# Revit family: Haworth_JiveTable_HalfPebbleLegs
name_source: partatom
category: Furniture Systems
revit_build: Autodesk Revit 2018 (Build: 20170223_1515(x64)
units: mm (PartAtom-declared; Revit-internal decimal feet)

## family parameters
Always vertical = Yes
Cut with Voids When Loaded = No
OmniClass Number = 23.40.70.14.64.21
OmniClass Title = Systems Furniture
Part Type = Normal
Room Calculation Point = No
Round Connector Dimension = Use Diameter
Shared = No
Work Plane-Based = No

## types (16) — shared parameters
Actual Height = 29"
Assembly Code = E2020200
Custom Size = No
Height = 29"
Leg Height = 27 13/16"
Manufacturer = Haworth, Inc.
Max. Depth = 60"
Max. Height = 29"
Max. Width = 60"
Min. Depth = 42"
Min. Height = 29"
Min. Width = 42"
Model = Haworth Jive
Revision Number = 0
Size = Verify Final Dim. w/ Haworth
Standard Depths = 42, 48, 54, 60 in.
Standard Heights = 29 in.
Standard Widths = 42, 48, 54, 60 in.
Table Thickness = 1 3/16"
URL = http://www.haworth.com
URL - Product = http://www.haworth.com
Warranty = http://www.haworth.com

## per-type parameters (varying)
| type | Actual Depth | Actual Width | Casters | Close Legs | Depth | Description | Far Legs | Glides | Post Extruded Base | Post Round Base | Table Radius | Vert. Leg Center | Width |
| 42d 42w 29h - Post Extruded Base - With Glides | 42" | 42" | No | 7" | 42" | Haworth Jive Table Half Pebble Legs - 42d 42w 29h - Post Extruded Bases - With Glides | 31" | Yes | Yes | No | 21" | 11" | 42" |
| 42d 42w 29h - Post Extruded Base - With Casters | 42" | 42" | Yes | 7" | 42" | Haworth Jive Table Half Pebble Legs - 42d 42w 29h - Post Extruded Base - With Casters | 31" | No | Yes | No | 21" | 11" | 42" |
| 48d 48w 29h - Post Extruded Base - With Glides | 48" | 48" | No | 8" | 48" | Haworth Jive Table Half Pebble Legs - 48d 48w 29h - Post Extruded Base - With Glides | 36" | Yes | Yes | No | 24" | 15" | 48" |
| 48d 48w 29h - Post Extruded Base - With Casters | 48" | 48" | Yes | 8" | 48" | Haworth Jive Table Half Pebble Legs - 48d 48w 29h - Post Extruded Base - With Casters | 36" | No | Yes | No | 24" | 15" | 48" |
| 54d 54w 29h - Post Extruded Base - With Glides | 54" | 54" | No | 10" | 54" | Haworth Jive Table Half Pebble Legs - 54d 54w 29h - Post Extruded Base - With Glides | 41" | Yes | Yes | No | 27" | 17" | 54" |
| 60d 60w 29h - Post Extruded Base - With Glides | 60" | 60" | No | 11" | 60" | Haworth Jive Table Half Pebble Legs - 60d 60w 29h - Post Extruded Base - With Glides | 45" | Yes | Yes | No | 30" | 19" | 60" |
| 54d 54w 29h - Post Extruded Base - With Casters | 54" | 54" | Yes | 10" | 54" | Haworth Jive Table Half Pebble Legs - 54d 54w 29h - Post Extruded Base - With Casters | 41" | No | Yes | No | 27" | 17" | 54" |
| 60d 60w 29h - Post Extruded Base - With Casters | 60" | 60" | Yes | 11" | 60" | Haworth Jive Table Half Pebble Legs - 60d 60w 29h - Post Extruded Base - With Casters | 45" | No | Yes | No | 30" | 19" | 60" |
| 42d 42w 29h - Post Round Base - With Casters | 42" | 42" | Yes | 7" | 42" | Haworth Jive Table Half Pebble Legs - 42d 42w 29h - Post Round Base - With Casters | 31" | No | No | Yes | 21" | 11" | 42" |
| 42d 42w 29h - Post Round Base - With Glides | 42" | 42" | No | 7" | 42" | Haworth Jive Table Half Pebble Legs - 42d 42w 29h - Post Round Bases - With Glides | 31" | Yes | No | Yes | 21" | 11" | 42" |
| 48d 48w 29h - Post Round Base - With Casters | 48" | 48" | Yes | 8" | 48" | Haworth Jive Table Half Pebble Legs - 48d 48w 29h - Post Round Base - With Casters | 36" | No | No | Yes | 24" | 15" | 48" |
| 48d 48w 29h - Post Round Base - With Glides | 48" | 48" | No | 8" | 48" | Haworth Jive Table Half Pebble Legs - 48d 48w 29h - Post Round Base - With Glides | 36" | Yes | No | Yes | 24" | 15" | 48" |
| 54d 54w 29h - Post Round Base - With Casters | 54" | 54" | Yes | 10" | 54" | Haworth Jive Table Half Pebble Legs - 54d 54w 29h - Post Round Base - With Casters | 41" | No | No | Yes | 27" | 17" | 54" |
| 54d 54w 29h - Post Round Base - With Glides | 54" | 54" | No | 10" | 54" | Haworth Jive Table Half Pebble Legs - 54d 54w 29h - Post Round Base - With Glides | 41" | Yes | No | Yes | 27" | 17" | 54" |
| 60d 60w 29h - Post Round Base - With Casters | 60" | 60" | Yes | 11" | 60" | Haworth Jive Table Half Pebble Legs - 60d 60w 29h - Post Round Base - With Casters | 45" | No | No | Yes | 30" | 19" | 60" |
| 60d 60w 29h - Post Round Base - With Glides | 60" | 60" | No | 11" | 60" | Haworth Jive Table Half Pebble Legs - 60d 60w 29h - Post Round Base - With Glides | 45" | Yes | No | Yes | 30" | 19" | 60" |

## geometry (parser evidence)
native form markers: Sweep x32
no freeform markers — native parametric forms only
